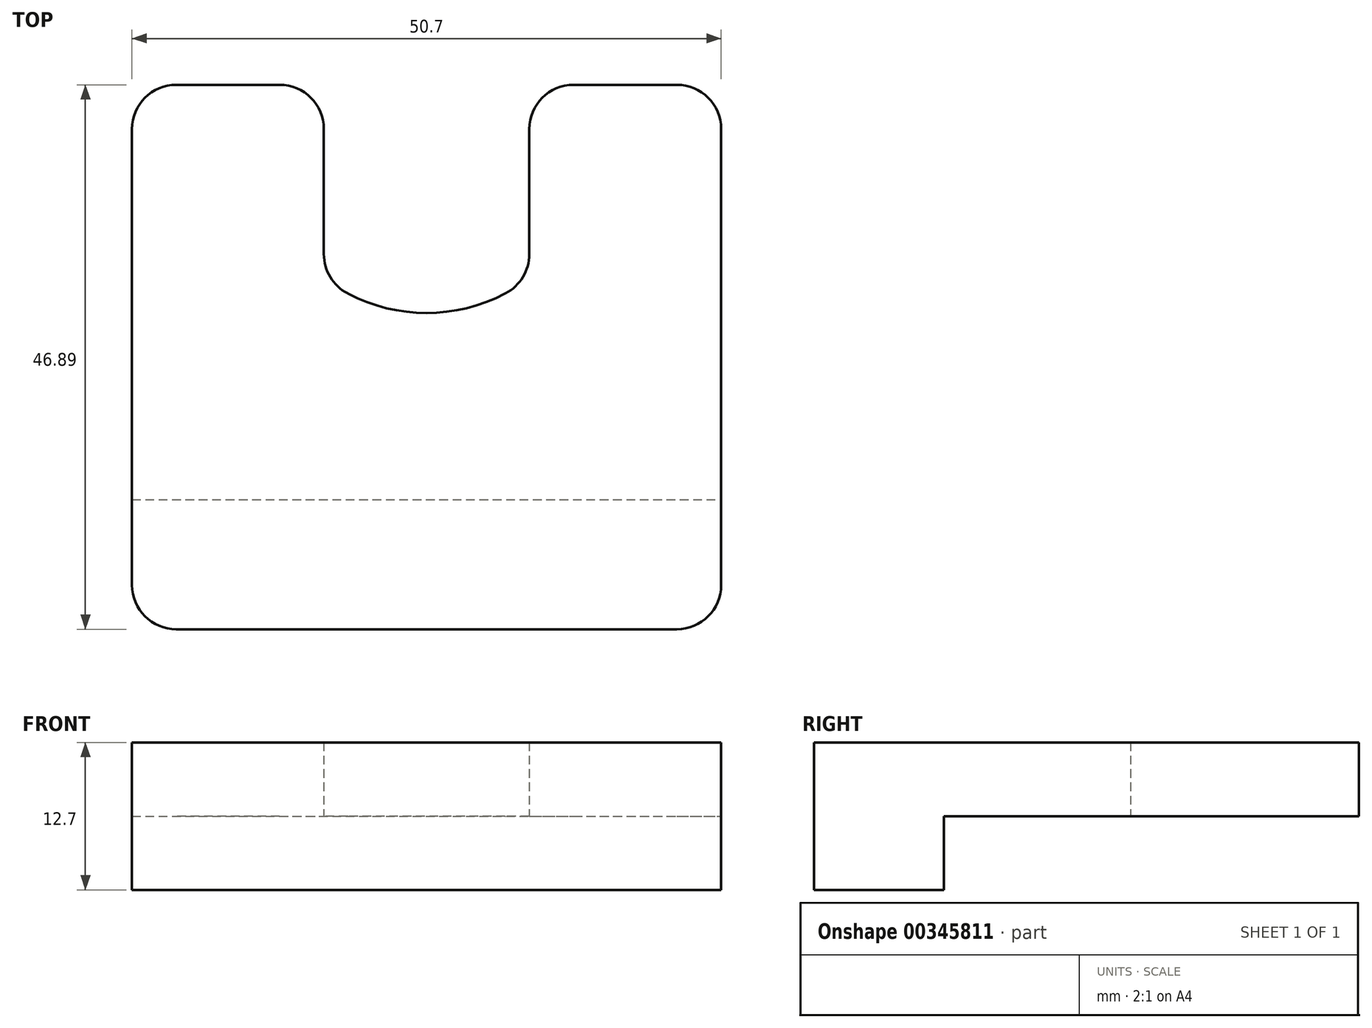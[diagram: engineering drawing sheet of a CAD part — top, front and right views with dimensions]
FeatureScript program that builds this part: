
annotation { "Feature Type Name" : "Feature", "Feature Type Description" : "" }
export const myFeature = defineFeature(function(context is Context, id is Id, definition is map)
    precondition{}
    {
        {
            var Q0;
            Q0=qCreatedBy(makeId("Top.planeOp"),FACE);
            var sketch = newSketch(context, id + "F0", { "sketchPlane" : qUnion([Q0])});
            skLineSegment(sketch, "E0", {"start": v(0, -25.35) * mm, "end": v(21.54, -25.35) * mm});
            skLineSegment(sketch, "E1", {"start": v(0, -25.35) * mm, "end": v(-21.54, -25.35) * mm});
            skLineSegment(sketch, "E2", {"start": v(-25.35, -21.54) * mm, "end": v(-25.35, 17.73) * mm});
            skLineSegment(sketch, "E3", {"start": v(25.35, -21.54) * mm, "end": v(25.35, 17.73) * mm});
            skPoint(sketch, "E4.visualSharp", {"position": v(-25.35, -25.35) * mm});
            skArc(sketch, "E4.filletArc", {"start": v(-25.35, -21.54) * mm, "mid": v(-24.24, -24.24) * mm, "end": v(-21.54, -25.35) * mm});
            skPoint(sketch, "E5.visualSharp", {"position": v(25.35, -25.35) * mm});
            skArc(sketch, "E5.filletArc", {"start": v(21.54, -25.35) * mm, "mid": v(24.24, -24.24) * mm, "end": v(25.35, -21.54) * mm});
            skLineSegment(sketch, "E6", {"start": v(-21.54, 21.54) * mm, "end": v(-12.65, 21.54) * mm});
            skLineSegment(sketch, "E7", {"start": v(21.54, 21.54) * mm, "end": v(12.65, 21.54) * mm});
            skLineSegment(sketch, "E8", {"start": v(8.84, 17.73) * mm, "end": v(8.84, 6.95) * mm});
            skLineSegment(sketch, "E9", {"start": v(-8.84, 17.73) * mm, "end": v(-8.84, 6.95) * mm});
            skPoint(sketch, "E10.visualSharp", {"position": v(-25.35, 21.54) * mm});
            skArc(sketch, "E10.filletArc", {"start": v(-21.54, 21.54) * mm, "mid": v(-24.24, 20.43) * mm, "end": v(-25.35, 17.73) * mm});
            skPoint(sketch, "E11.visualSharp", {"position": v(-8.84, 21.54) * mm});
            skArc(sketch, "E11.filletArc", {"start": v(-8.84, 17.73) * mm, "mid": v(-9.95, 20.43) * mm, "end": v(-12.65, 21.54) * mm});
            skPoint(sketch, "E12.visualSharp", {"position": v(8.84, 21.54) * mm});
            skArc(sketch, "E12.filletArc", {"start": v(12.65, 21.54) * mm, "mid": v(9.95, 20.43) * mm, "end": v(8.84, 17.73) * mm});
            skPoint(sketch, "E13.visualSharp", {"position": v(25.35, 21.54) * mm});
            skArc(sketch, "E13.filletArc", {"start": v(25.35, 17.73) * mm, "mid": v(24.24, 20.43) * mm, "end": v(21.54, 21.54) * mm});
            skLineSegment(sketch, "E14", {"start": v(-6.8, 3.58) * mm, "end": v(-6.74, 3.55) * mm});
            skLineSegment(sketch, "E15", {"start": v(6.8, 3.58) * mm, "end": v(6.74, 3.55) * mm});
            skPoint(sketch, "E16.visualSharp", {"position": v(8.84, 4.65) * mm});
            skArc(sketch, "E16.filletArc", {"start": v(6.8, 3.58) * mm, "mid": v(8.29, 4.98) * mm, "end": v(8.84, 6.95) * mm});
            skPoint(sketch, "E17.visualSharp", {"position": v(0, 0) * mm});
            skArc(sketch, "E17.filletArc", {"start": v(-6.74, 3.55) * mm, "mid": v(0, 1.88) * mm, "end": v(6.74, 3.55) * mm});
            skPoint(sketch, "E18.visualSharp", {"position": v(-8.84, 4.65) * mm});
            skArc(sketch, "E18.filletArc", {"start": v(-8.84, 6.95) * mm, "mid": v(-8.29, 4.98) * mm, "end": v(-6.8, 3.58) * mm});
            skSolve(sketch);
        }
        {
            var Q0;
            Q0 = qSketchRegion(id + "F0", true);
            extrude(context, id + "F1", {"entities" : qUnion([Q0]), "depth" : 12.7 * mm});
        }
        {
            var Q0;
            Q0=makeQuery(id+"F1.opExtrude","SWEPT_FACE",FACE,{"disambiguationData":[OSD([sQuery(id+"F0.wireOp",EDGE,"E3")])]});
            var sketch = newSketch(context, id + "F2", { "sketchPlane" : qUnion([Q0])});
            skLineSegment(sketch, "E19", {"start": v(-14.2, 0) * mm, "end": v(-14.2, 6.35) * mm});
            skLineSegment(sketch, "E20", {"start": v(-14.2, 6.35) * mm, "end": v(36.23, 6.35) * mm});
            skLineSegment(sketch, "E21", {"start": v(36.23, 6.35) * mm, "end": v(36.23, 0) * mm});
            skLineSegment(sketch, "E22", {"start": v(36.23, 0) * mm, "end": v(-14.2, 0) * mm});
            skSolve(sketch);
        }
        {
            var Q0;
            Q0 = qSketchRegion(id + "F2", true);
            extrude(context, id + "F3", {"entities" : qUnion([Q0]), "operationType" : NewBodyOperationType.REMOVE, "oppositeDirection" : true, "depth" : 58.42 * mm});
        }
    });
